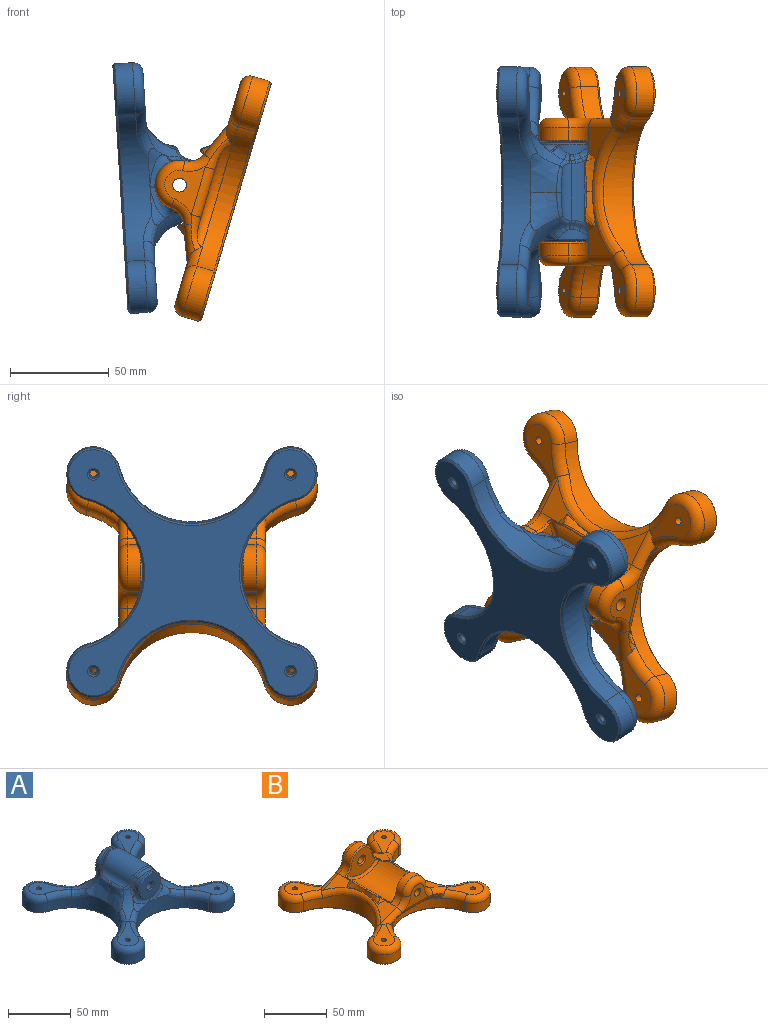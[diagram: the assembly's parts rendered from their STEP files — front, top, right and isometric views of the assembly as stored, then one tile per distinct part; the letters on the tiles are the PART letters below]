
ASSEMBLY  parts=2 mates=1
PART A: 133 faces, bbox 129.2x129.2x44 mm
  f0: bspline ~26.85x25mm, area 66.7mm2, adj f6,f8,f14,f47,f104,f106
  f1: bspline ~26.85x25mm, area 255.7mm2, adj f3,f4,f20,f34,f91,f95
  f2: bspline ~26.85x25mm, area 66.7mm2, adj f5,f7,f18,f32,f119,f121
  f3: bspline ~27.14x25mm, area 260mm2, adj f1,f5,f20,f29,f97,f100
  f4: torus R=45mm, axis (0,0,1), area 182.4mm2, adj f1,f6,f12,f34,f38,f90,f105,f107
  f5: torus R=45mm, axis (0,0,1), area 182.4mm2, adj f2,f3,f13,f29,f32,f102,f121,f123
  f6: bspline ~27.14x16.67mm, area 67.1mm2, adj f0,f4,f14,f38,f103,f105
  f7: bspline ~27.14x16.67mm, area 67.1mm2, adj f2,f9,f18,f39,f118,f120
  f8: torus R=45mm, axis (0,0,1), area 182.4mm2, adj f0,f11,f28,f44,f47,f74,f106,f108
  f9: torus R=45mm, axis (0,0,1), area 182.4mm2, adj f7,f10,f26,f39,f42,f85,f120,f122
  f10: bspline ~26.85x25mm, area 255.7mm2, adj f9,f16,f28,f42,f80,f82
  f11: plane 27.75x27.75mm, normal (0,0,1), area 316.6mm2, adj f8,f21,f45,f46,f48
  f12: plane 27.75x27.75mm, normal (0,0,1), area 316.6mm2, adj f4,f25,f35,f36,f37
  f13: plane 27.75x27.75mm, normal (0,0,1), area 316.6mm2, adj f5,f23,f30,f31,f33
  f14: cylinder r=38.22mm len=73.9mm, axis (0,0,-1), area 1128.3mm2, adj f0,f6,f15,f24,f37,f38,f47,f48
  f15: cylinder r=13.5mm len=26.55mm, axis (0,0,-1), area 509.8mm2, adj f14,f16,f46,f60
  f16: cylinder r=38.22mm len=73.9mm, axis (0,0,-1), area 1128.3mm2, adj f10,f15,f17,f28,f42,f43,f44,f45
  f17: cylinder r=13.5mm len=26.55mm, axis (0,0,-1), area 509.8mm2, adj f16,f18,f41,f64
  f18: cylinder r=38.22mm len=73.9mm, axis (0,0,-1), area 1128.3mm2, adj f2,f7,f17,f19,f32,f33,f39,f40
  f19: cylinder r=13.5mm len=26.55mm, axis (0,0,-1), area 509.8mm2, adj f18,f20,f31,f63
  f20: cylinder r=38.22mm len=73.9mm, axis (0,0,-1), area 1128.3mm2, adj f1,f3,f19,f24,f29,f30,f34,f35
  f21: cylinder r=2mm len=14mm, axis (0,0,-1), area 175.9mm2, adj f11,f67
  f22: cylinder r=2mm len=14mm, axis (0,0,-1), area 175.9mm2, adj f26,f68
  f23: cylinder r=2mm len=14mm, axis (0,0,-1), area 175.9mm2, adj f13,f69
  f24: cylinder r=13.5mm len=26.55mm, axis (0,0,-1), area 509.8mm2, adj f14,f20,f36,f59
  f25: cylinder r=2mm len=14mm, axis (0,0,-1), area 175.9mm2, adj f12,f66
  f26: plane 27.75x27.75mm, normal (0,0,1), area 316.6mm2, adj f9,f22,f40,f41,f43
  f27: plane 125x125mm, normal (0,0,-1), area 5767.8mm2, adj f58,f59,f60,f61,f62,f63,f64,f65
  f28: bspline ~27.14x25mm, area 260mm2, adj f8,f10,f16,f44,f73,f78
  f29: bspline ~18.12x11.7mm, area 108.5mm2, adj f3,f5,f20,f30
  f30: torus R=43.22mm, axis (0,0,1), area 163.7mm2, adj f13,f20,f29,f31
  f31: torus R=8.5mm, axis (0,0,1), area 385mm2, adj f13,f19,f30,f33
  f32: bspline ~19.27x13.05mm, area 108.5mm2, adj f2,f5,f18,f33
  f33: torus R=43.22mm, axis (0,0,1), area 163.7mm2, adj f13,f18,f31,f32
  f34: bspline ~19.27x13.05mm, area 108.5mm2, adj f1,f4,f20,f35
  f35: torus R=43.22mm, axis (0,0,1), area 163.7mm2, adj f12,f20,f34,f36
  f36: torus R=8.5mm, axis (0,0,1), area 385mm2, adj f12,f24,f35,f37
  f37: torus R=43.22mm, axis (0,0,1), area 163.7mm2, adj f12,f14,f36,f38
  f38: bspline ~18.12x11.7mm, area 108.5mm2, adj f4,f6,f14,f37
  f39: bspline ~18.12x11.7mm, area 108.5mm2, adj f7,f9,f18,f40
  f40: torus R=43.22mm, axis (0,0,1), area 163.7mm2, adj f18,f26,f39,f41
  f41: torus R=8.5mm, axis (0,0,1), area 385mm2, adj f17,f26,f40,f43
  f42: bspline ~19.27x13.05mm, area 108.5mm2, adj f9,f10,f16,f43
  f43: torus R=43.22mm, axis (0,0,1), area 163.7mm2, adj f16,f26,f41,f42
  f44: bspline ~19.27x13.05mm, area 108.5mm2, adj f8,f16,f28,f45
  f45: torus R=43.22mm, axis (0,0,1), area 163.7mm2, adj f11,f16,f44,f46
  f46: torus R=8.5mm, axis (0,0,1), area 385mm2, adj f11,f15,f45,f48
  f47: bspline ~19.27x13.05mm, area 108.5mm2, adj f0,f8,f14,f48
  f48: torus R=43.22mm, axis (0,0,1), area 163.7mm2, adj f11,f14,f46,f47
  f49: plane 23x23mm, normal (0,1,0), area 351.9mm2, adj f54,f55
  f50: cylinder r=12.5mm len=25mm, axis (0,-1,0), area 142.8mm2, adj f54,f120,f121,f122,f123,f124,f125,f126
  f51: cylinder r=12.5mm len=25mm, axis (0,-1,0), area 142.8mm2, adj f57,f105,f106,f107,f108,f109,f110,f111
  f52: plane 23x23mm, normal (0,-1,0), area 351.9mm2, adj f56,f57
  f53: cylinder r=3.5mm len=48mm, axis (0,1,0), area 1055.6mm2, adj f55,f56
  f54: cone r=12.5mm half-angle=45deg, axis (0,-1,0), area 106.6mm2, adj f49,f50,f118,f119
  f55: cone r=4.5mm half-angle=45deg, axis (0,1,0), area 35.5mm2, adj f49,f53
  f56: cone r=3.5mm half-angle=45deg, axis (0,-1,0), area 35.5mm2, adj f52,f53
  f57: cone r=11.5mm half-angle=45deg, axis (0,1,0), area 106.6mm2, adj f51,f52,f103,f104
  f58: cone r=39.22mm half-angle=45deg, axis (0,0,-1), area 143.7mm2, adj f14,f27,f59,f60
  f59: cone r=13.5mm half-angle=45deg, axis (0,0,1), area 77.1mm2, adj f24,f27,f58,f61
  f60: cone r=13.5mm half-angle=45deg, axis (0,0,1), area 77.1mm2, adj f15,f27,f58,f62
  f61: cone r=39.22mm half-angle=45deg, axis (0,0,-1), area 143.7mm2, adj f20,f27,f59,f63
  f62: cone r=39.22mm half-angle=45deg, axis (0,0,-1), area 143.7mm2, adj f16,f27,f60,f64
  f63: cone r=13.5mm half-angle=45deg, axis (0,0,1), area 77.1mm2, adj f19,f27,f61,f65
  f64: cone r=13.5mm half-angle=45deg, axis (0,0,1), area 77.1mm2, adj f17,f27,f62,f65
  f65: cone r=39.22mm half-angle=45deg, axis (0,0,-1), area 143.7mm2, adj f18,f27,f63,f64
  f66: cone r=3mm half-angle=45deg, axis (0,0,-1), area 22.2mm2, adj f25,f27
  f67: cone r=3mm half-angle=45deg, axis (0,0,-1), area 22.2mm2, adj f21,f27
  f68: cone r=3mm half-angle=45deg, axis (0,0,-1), area 22.2mm2, adj f22,f27
  f69: cone r=3mm half-angle=45deg, axis (0,0,-1), area 22.2mm2, adj f23,f27
  f70: cylinder r=14mm len=34.81mm, axis (0,-1,0), area 1095.8mm2, adj f71,f72,f77,f79,f81,f84,f86,f89
  f71: cylinder r=7mm len=28.77mm, axis (0,-1,0), area 176.4mm2, adj f70,f74,f75,f78,f80,f85,f87
  f72: cylinder r=7mm len=28.77mm, axis (0,-1,0), area 176.4mm2, adj f70,f88,f90,f95,f97,f101,f102
  f73: bspline ~0.23x0.16mm, area 0mm2, adj f28,f74,f76
  f74: bspline ~7.1x6.35mm, area 15.6mm2, adj f8,f71,f73,f75,f76,f110
  f75: bspline ~2.53x1.82mm, area 1.4mm2, adj f71,f74,f77,f112
  f76: bspline ~1.51x1.46mm, area 0.2mm2, adj f73,f74,f78
  f77: bspline ~3.8x2.9mm, area 4.1mm2, adj f70,f75,f79,f114
  f78: bspline ~13.3x3.11mm, area 40mm2, adj f28,f71,f76,f80
  f79: bspline ~6.42x4.63mm, area 8.8mm2, adj f70,f77,f81,f116
  f80: bspline ~15.17x3.12mm, area 39.5mm2, adj f10,f71,f78,f83
  f81: bspline ~20.82x6.37mm, area 39.9mm2, adj f70,f79,f84,f117
  f82: bspline ~0.22x0.16mm, area 0mm2, adj f10,f83,f85
  f83: bspline ~1.52x1.46mm, area 0.2mm2, adj f80,f82,f85
  f84: bspline ~6.42x4.62mm, area 8.8mm2, adj f70,f81,f86,f115
  f85: bspline ~7.1x6.35mm, area 15.6mm2, adj f9,f71,f82,f83,f87,f124
  f86: bspline ~4.1x2.99mm, area 4.1mm2, adj f70,f84,f88,f113
  f87: bspline ~2.53x1.8mm, area 1.4mm2, adj f71,f85,f89,f126
  f88: bspline ~2.53x1.8mm, area 1.4mm2, adj f72,f86,f90,f111
  f89: bspline ~4.1x2.99mm, area 4.1mm2, adj f70,f87,f92,f128
  f90: bspline ~7.1x6.35mm, area 15.6mm2, adj f4,f72,f88,f91,f93,f109
  f91: bspline ~0.22x0.16mm, area 0mm2, adj f1,f90,f93
  f92: bspline ~6.42x4.62mm, area 8.8mm2, adj f70,f89,f94,f130
  f93: bspline ~1.52x1.46mm, area 0.2mm2, adj f90,f91,f95
  f94: bspline ~20.82x6.37mm, area 39.9mm2, adj f70,f92,f96,f132
  f95: bspline ~15.17x3.12mm, area 39.5mm2, adj f1,f72,f93,f97
  f96: bspline ~6.42x4.63mm, area 8.8mm2, adj f70,f94,f98,f131
  f97: bspline ~16.05x3.16mm, area 40mm2, adj f3,f72,f95,f99
  f98: bspline ~3.8x2.9mm, area 4.1mm2, adj f70,f96,f101,f129
  f99: bspline ~1.51x1.46mm, area 0.2mm2, adj f97,f100,f102
  f100: bspline ~0.23x0.16mm, area 0mm2, adj f3,f99,f102
  f101: bspline ~2.53x1.82mm, area 1.4mm2, adj f72,f98,f102,f127
  f102: bspline ~7.1x6.35mm, area 15.6mm2, adj f5,f72,f99,f100,f101,f125
  f103: bspline ~16.65x13.39mm, area 75.1mm2, adj f6,f57,f104,f105
  f104: bspline ~16.24x13.4mm, area 74.3mm2, adj f0,f57,f103,f106
  f105: bspline ~5.11x4.6mm, area 5.2mm2, adj f4,f6,f51,f103,f107
  f106: bspline ~5.41x4.82mm, area 5.2mm2, adj f0,f8,f51,f104,f108
  f107: bspline ~10.08x9.28mm, area 31.6mm2, adj f4,f51,f105,f109
  f108: bspline ~9.96x8.71mm, area 31.6mm2, adj f8,f51,f106,f110
  f109: bspline ~3.84x3.78mm, area 7.8mm2, adj f51,f90,f107,f111
  f110: bspline ~4.01x3.82mm, area 7.8mm2, adj f51,f74,f108,f112
  f111: bspline ~3.06x1.79mm, area 2mm2, adj f51,f88,f109,f113
  f112: bspline ~2.99x1.29mm, area 2mm2, adj f51,f75,f110,f114
  f113: bspline ~3.39x3.14mm, area 5.5mm2, adj f51,f86,f111,f115
  f114: bspline ~3.19x3.12mm, area 5.5mm2, adj f51,f77,f112,f116
  f115: bspline ~5.06x3.94mm, area 12mm2, adj f51,f84,f113,f117
  f116: bspline ~5.3x4.06mm, area 12mm2, adj f51,f79,f114,f117
  f117: bspline ~20.7x5.99mm, area 63.9mm2, adj f51,f81,f115,f116
  f118: bspline ~16.65x13.39mm, area 75.1mm2, adj f7,f54,f119,f120
  f119: bspline ~16.24x13.4mm, area 74.3mm2, adj f2,f54,f118,f121
  f120: bspline ~5.11x4.6mm, area 5.2mm2, adj f7,f9,f50,f118,f122
  f121: bspline ~5.41x4.82mm, area 5.2mm2, adj f2,f5,f50,f119,f123
  f122: bspline ~10.08x9.28mm, area 31.6mm2, adj f9,f50,f120,f124
  f123: bspline ~9.96x8.71mm, area 31.6mm2, adj f5,f50,f121,f125
  f124: bspline ~3.84x3.78mm, area 7.8mm2, adj f50,f85,f122,f126
  f125: bspline ~4.01x3.82mm, area 7.8mm2, adj f50,f102,f123,f127
  f126: bspline ~3.06x1.79mm, area 2mm2, adj f50,f87,f124,f128
  f127: bspline ~2.99x1.29mm, area 2mm2, adj f50,f101,f125,f129
  f128: bspline ~3.39x3.14mm, area 5.5mm2, adj f50,f89,f126,f130
  f129: bspline ~3.19x3.12mm, area 5.5mm2, adj f50,f98,f127,f131
  f130: bspline ~5.06x3.94mm, area 12mm2, adj f50,f92,f128,f132
  f131: bspline ~5.3x4.06mm, area 12mm2, adj f50,f96,f129,f132
  f132: bspline ~19.93x5.99mm, area 63.9mm2, adj f50,f94,f130,f131
PART B: 112 faces, bbox 129.8x129.8x44.1 mm
  f0: cylinder r=12.5mm len=24.93mm, axis (0,-1,0), area 243.1mm2, adj f54,f55,f65,f91
  f1: cylinder r=3.5mm len=11.5mm, axis (0,1,0), area 252.9mm2, adj f15,f102
  f2: plane 65.16x18.1mm, normal (0.38,0,0.93), area 377.8mm2, adj f8,f9,f10,f11,f53,f54,f56,f58
  f3: plane 65.16x18.1mm, normal (-0.38,0,0.93), area 377.8mm2, adj f4,f5,f6,f7,f52,f55,f57,f62
  f4: bspline ~26.85x25mm, area 62.8mm2, adj f3,f5,f6,f106
  f5: bspline ~27.14x25mm, area 63.8mm2, adj f3,f4,f7,f105
  f6: torus R=45mm, axis (0,0,1), area 12.9mm2, adj f3,f4,f107
  f7: torus R=45mm, axis (0,0,1), area 12.9mm2, adj f3,f5,f104
  f8: bspline ~26.85x25mm, area 62.8mm2, adj f2,f10,f11,f110
  f9: torus R=45mm, axis (0,0,1), area 12.9mm2, adj f2,f11,f108
  f10: torus R=45mm, axis (0,0,1), area 12.9mm2, adj f2,f8,f111
  f11: bspline ~27.14x25mm, area 63.8mm2, adj f2,f8,f9,f109
  f12: cylinder r=12.5mm len=24.93mm, axis (0,-1,0), area 243.1mm2, adj f56,f57,f60,f98
  f13: cylinder r=3.5mm len=11.5mm, axis (0,1,0), area 252.9mm2, adj f14,f103
  f14: plane 26.06x17.5mm, normal (0,-1,0), area 238.2mm2, adj f13,f59,f60,f61,f71,f72,f73
  f15: plane 26.06x17.5mm, normal (0,1,0), area 238.2mm2, adj f1,f64,f65,f66,f68,f69,f70
  f16: plane 25.29x2.5mm, normal (0,0,-1), area 42.5mm2, adj f38,f72
  f17: plane 25.29x2.5mm, normal (0,0,-1), area 42.5mm2, adj f39,f69
  f18: cylinder r=2mm len=14mm, axis (0,0,-1), area 175.9mm2, adj f34,f83
  f19: cylinder r=2mm len=14mm, axis (0,0,-1), area 175.9mm2, adj f33,f82
  f20: cylinder r=2mm len=14mm, axis (0,0,-1), area 175.9mm2, adj f31,f85
  f21: cylinder r=2mm len=14mm, axis (0,0,-1), area 175.9mm2, adj f29,f84
  f22: cylinder r=13.5mm len=26.55mm, axis (0,0,-1), area 509.8mm2, adj f30,f32,f41,f75
  f23: cylinder r=13.5mm len=26.55mm, axis (0,0,-1), area 509.8mm2, adj f27,f30,f44,f79
  f24: cylinder r=13.5mm len=26.55mm, axis (0,0,-1), area 509.8mm2, adj f28,f32,f50,f76
  f25: cylinder r=13.5mm len=26.55mm, axis (0,0,-1), area 509.8mm2, adj f27,f28,f47,f80
  f26: plane 125x125mm, normal (0,0,-1), area 5767.8mm2, adj f74,f75,f76,f77,f78,f79,f80,f81
  f27: cylinder r=38.22mm len=73.9mm, axis (0,0,-1), area 902.8mm2, adj f23,f25,f39,f45,f46,f81
  f28: cylinder r=38.22mm len=73.9mm, axis (0,0,-1), area 1192.5mm2, adj f24,f25,f48,f49,f53,f78
  f29: plane 25.59x25.15mm, normal (0,0,1), area 302.2mm2, adj f21,f46,f47,f48,f63
  f30: cylinder r=38.22mm len=73.9mm, axis (0,0,-1), area 1192.5mm2, adj f22,f23,f42,f43,f52,f77
  f31: plane 25.59x25.15mm, normal (0,0,1), area 302.2mm2, adj f20,f43,f44,f45,f67
  f32: cylinder r=38.22mm len=73.9mm, axis (0,0,-1), area 902.8mm2, adj f22,f24,f38,f40,f51,f74
  f33: plane 25.59x25.15mm, normal (0,0,1), area 302.2mm2, adj f19,f40,f41,f42,f62
  f34: plane 25.59x25.15mm, normal (0,0,1), area 302.2mm2, adj f18,f49,f50,f51,f58
  f35: cylinder r=25mm len=46mm, axis (0,-1,0), area 1996.7mm2, adj f86,f87,f88,f94,f95,f101,f104,f105
  f36: plane 31.16x24.5mm, normal (0,-1,0), area 454mm2, adj f86,f90,f91,f92,f102
  f37: plane 31.16x24.5mm, normal (0,1,0), area 454mm2, adj f87,f97,f98,f99,f103
  f38: torus R=33.22mm, axis (0,0,-1), area 337.3mm2, adj f16,f32,f71,f73
  f39: torus R=33.22mm, axis (0,0,-1), area 337.3mm2, adj f17,f27,f68,f70
  f40: torus R=43.22mm, axis (0,0,1), area 145.4mm2, adj f32,f33,f41,f62,f71
  f41: torus R=8.5mm, axis (0,0,1), area 385mm2, adj f22,f33,f40,f42
  f42: torus R=43.22mm, axis (0,0,1), area 130.1mm2, adj f30,f33,f41,f52,f62
  f43: torus R=43.22mm, axis (0,0,1), area 130.1mm2, adj f30,f31,f44,f52,f67
  f44: torus R=8.5mm, axis (0,0,1), area 385mm2, adj f23,f31,f43,f45
  f45: torus R=43.22mm, axis (0,0,1), area 145.4mm2, adj f27,f31,f44,f67,f68
  f46: torus R=43.22mm, axis (0,0,1), area 145.4mm2, adj f27,f29,f47,f63,f70
  f47: torus R=8.5mm, axis (0,0,1), area 385mm2, adj f25,f29,f46,f48
  f48: torus R=43.22mm, axis (0,0,1), area 130.1mm2, adj f28,f29,f47,f53,f63
  f49: torus R=43.22mm, axis (0,0,1), area 130.1mm2, adj f28,f34,f50,f53,f58
  f50: torus R=8.5mm, axis (0,0,1), area 385mm2, adj f24,f34,f49,f51
  f51: torus R=43.22mm, axis (0,0,1), area 145.4mm2, adj f32,f34,f50,f58,f73
  f52: bspline ~67.1x17.43mm, area 447.2mm2, adj f3,f30,f42,f43,f62,f67
  f53: bspline ~67.1x17.43mm, area 447.2mm2, adj f2,f28,f48,f49,f58,f63
  f54: cylinder r=10mm len=12.69mm, axis (0,-1,0), area 74.2mm2, adj f0,f2,f64,f88,f89,f90,f111
  f55: cylinder r=10mm len=12.69mm, axis (0,-1,0), area 74.2mm2, adj f0,f3,f66,f92,f93,f94,f104
  f56: cylinder r=10mm len=12.69mm, axis (0,-1,0), area 74.2mm2, adj f2,f12,f59,f99,f100,f101,f108
  f57: cylinder r=10mm len=12.69mm, axis (0,-1,0), area 74.2mm2, adj f3,f12,f61,f95,f96,f97,f107
  f58: cylinder r=5mm len=20.6mm, axis (0.93,0,-0.38), area 113.9mm2, adj f2,f34,f49,f51,f53,f59,f73
  f59: torus R=15mm, axis (0,-1,0), area 100.8mm2, adj f14,f56,f58,f60,f73
  f60: torus R=7.5mm, axis (0,-1,0), area 251mm2, adj f12,f14,f59,f61
  f61: torus R=15mm, axis (0,-1,0), area 100.8mm2, adj f14,f57,f60,f62,f71
  f62: cylinder r=5mm len=20.6mm, axis (0.93,0,0.38), area 113.9mm2, adj f3,f33,f40,f42,f52,f61,f71
  f63: cylinder r=5mm len=20.6mm, axis (-0.93,0,0.38), area 113.9mm2, adj f2,f29,f46,f48,f53,f64,f70
  f64: torus R=15mm, axis (0,-1,0), area 100.8mm2, adj f15,f54,f63,f65,f70
  f65: torus R=7.5mm, axis (0,-1,0), area 251mm2, adj f0,f15,f64,f66
  f66: torus R=15mm, axis (0,-1,0), area 100.8mm2, adj f15,f55,f65,f67,f68
  f67: cylinder r=5mm len=20.6mm, axis (-0.93,0,-0.38), area 113.9mm2, adj f3,f31,f43,f45,f52,f66,f68
  f68: bspline ~21.34x10.5mm, area 83mm2, adj f15,f39,f45,f66,f67,f69
  f69: cylinder r=5mm len=25.29mm, axis (1,0,0), area 198.6mm2, adj f15,f17,f68,f70
  f70: bspline ~21.34x10.5mm, area 83mm2, adj f15,f39,f46,f63,f64,f69
  f71: bspline ~21.34x10.5mm, area 83mm2, adj f14,f38,f40,f61,f62,f72
  f72: cylinder r=5mm len=25.29mm, axis (-1,0,0), area 198.6mm2, adj f14,f16,f71,f73
  f73: bspline ~21.34x10.5mm, area 83mm2, adj f14,f38,f51,f58,f59,f72
  f74: cone r=39.22mm half-angle=45deg, axis (0,0,-1), area 143.7mm2, adj f26,f32,f75,f76
  f75: cone r=13.5mm half-angle=45deg, axis (0,0,1), area 77.1mm2, adj f22,f26,f74,f77
  f76: cone r=13.5mm half-angle=45deg, axis (0,0,1), area 77.1mm2, adj f24,f26,f74,f78
  f77: cone r=39.22mm half-angle=45deg, axis (0,0,-1), area 143.7mm2, adj f26,f30,f75,f79
  f78: cone r=39.22mm half-angle=45deg, axis (0,0,-1), area 143.7mm2, adj f26,f28,f76,f80
  f79: cone r=13.5mm half-angle=45deg, axis (0,0,1), area 77.1mm2, adj f23,f26,f77,f81
  f80: cone r=13.5mm half-angle=45deg, axis (0,0,1), area 77.1mm2, adj f25,f26,f78,f81
  f81: cone r=39.22mm half-angle=45deg, axis (0,0,-1), area 143.7mm2, adj f26,f27,f79,f80
  f82: cone r=3mm half-angle=45deg, axis (0,0,-1), area 22.2mm2, adj f19,f26
  f83: cone r=3mm half-angle=45deg, axis (0,0,-1), area 22.2mm2, adj f18,f26
  f84: cone r=3mm half-angle=45deg, axis (0,0,-1), area 22.2mm2, adj f21,f26
  f85: cone r=3mm half-angle=45deg, axis (0,0,-1), area 22.2mm2, adj f20,f26
  f86: torus R=23mm, axis (0,-1,0), area 116.2mm2, adj f35,f36,f89,f93
  f87: torus R=23mm, axis (0,-1,0), area 116.2mm2, adj f35,f37,f96,f100
  f88: plane 3.18x1.08mm, normal (-0.19,0,0.98), area 3.1mm2, adj f35,f54,f89,f111
  f89: bspline ~3.07x3mm, area 4.9mm2, adj f54,f86,f88,f90
  f90: cone r=11mm half-angle=45deg, axis (0,-1,0), area 12.2mm2, adj f36,f54,f89,f91
  f91: cone r=12.5mm half-angle=45deg, axis (0,1,0), area 50.8mm2, adj f0,f36,f90,f92
  f92: cone r=11mm half-angle=45deg, axis (0,-1,0), area 12.2mm2, adj f36,f55,f91,f93
  f93: bspline ~3.07x3mm, area 4.9mm2, adj f55,f86,f92,f94
  f94: plane 3.18x1.08mm, normal (0.19,0,0.98), area 3.1mm2, adj f35,f55,f93,f104
  f95: plane 3.18x1.08mm, normal (0.19,0,0.98), area 3.1mm2, adj f35,f57,f96,f107
  f96: bspline ~3.07x3mm, area 4.9mm2, adj f57,f87,f95,f97
  f97: cone r=11mm half-angle=45deg, axis (0,1,0), area 12.2mm2, adj f37,f57,f96,f98
  f98: cone r=11.5mm half-angle=45deg, axis (0,-1,0), area 50.8mm2, adj f12,f37,f97,f99
  f99: cone r=11mm half-angle=45deg, axis (0,1,0), area 12.2mm2, adj f37,f56,f98,f100
  f100: bspline ~3.07x3mm, area 4.9mm2, adj f56,f87,f99,f101
  f101: plane 3.18x1.08mm, normal (-0.19,0,0.98), area 3.1mm2, adj f35,f56,f100,f108
  f102: cone r=3.5mm half-angle=45deg, axis (0,-1,0), area 35.5mm2, adj f1,f36
  f103: cone r=4.5mm half-angle=45deg, axis (0,1,0), area 35.5mm2, adj f13,f37
  f104: bspline ~9.38x4.74mm, area 7mm2, adj f3,f7,f35,f55,f94,f105
  f105: bspline ~19.61x1.8mm, area 25.6mm2, adj f5,f35,f104,f106
  f106: bspline ~19.26x1.79mm, area 25.2mm2, adj f4,f35,f105,f107
  f107: bspline ~11.89x5.51mm, area 7mm2, adj f3,f6,f35,f57,f95,f106
  f108: bspline ~11.89x5.51mm, area 7mm2, adj f2,f9,f35,f56,f101,f109
  f109: bspline ~19.55x1.8mm, area 25.6mm2, adj f11,f35,f108,f110
  f110: bspline ~19.26x1.79mm, area 25.2mm2, adj f8,f35,f109,f111
  f111: bspline ~11.89x5.51mm, area 7mm2, adj f2,f10,f35,f54,f88,f110
PLACE A rot(axis=(0,1,0),86.5deg) t=(-179.66,-95.57,24.59)mm
PLACE B rot(axis=(0,-1,0),73.5deg) t=(-120.94,-95.57,17.95)mm
MATE cylindrical B.f1 <-> A.f50  axis (0,1,0) through (-149.71,-121.57,26.45)mm
